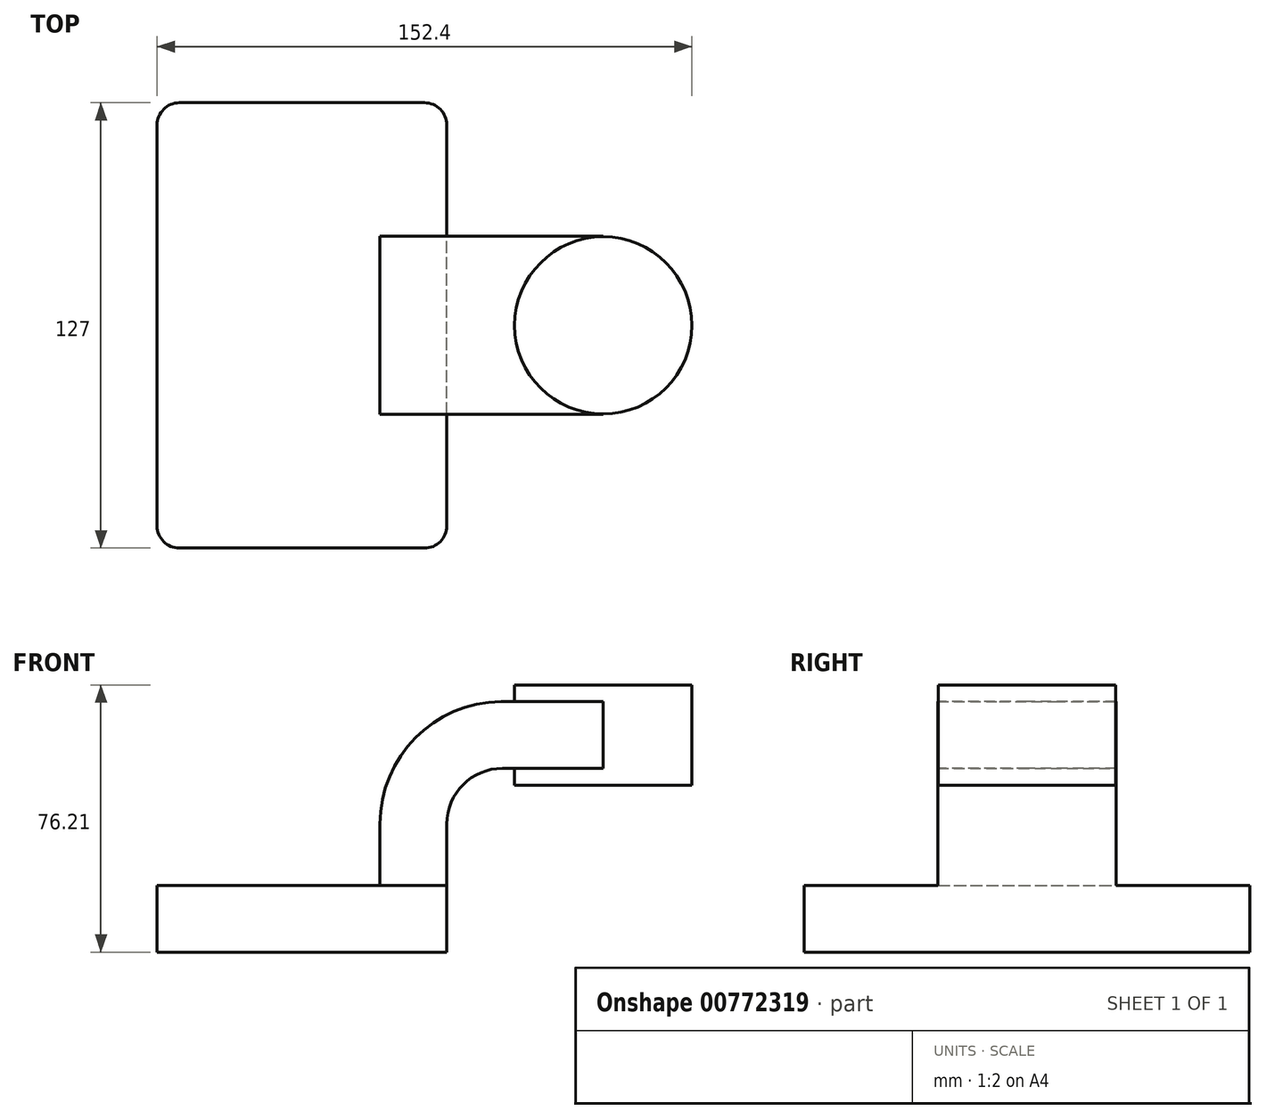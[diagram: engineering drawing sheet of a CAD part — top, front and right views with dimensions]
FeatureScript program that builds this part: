
annotation { "Feature Type Name" : "Feature", "Feature Type Description" : "" }
export const myFeature = defineFeature(function(context is Context, id is Id, definition is map)
    precondition{}
    {
        {
            var Q0;
            Q0=qCreatedBy(makeId("Front.planeOp"),FACE);
            var sketch = newSketch(context, id + "F0", { "sketchPlane" : qUnion([Q0])});
            skLineSegment(sketch, "E0.bottom", {"start": v(-41.28, 9.52) * mm, "end": v(41.27, 9.53) * mm});
            skLineSegment(sketch, "E0.top", {"start": v(-41.28, -9.52) * mm, "end": v(41.28, -9.52) * mm});
            skLineSegment(sketch, "E0.left", {"start": v(-41.28, 9.52) * mm, "end": v(-41.28, -9.53) * mm});
            skLineSegment(sketch, "E0.right", {"start": v(41.27, 9.53) * mm, "end": v(41.28, -9.52) * mm});
            skPoint(sketch, "E0.middle", {"position": v(0, 0) * mm});
            skLineSegment(sketch, "E1.bottom", {"start": v(60.32, 38.1) * mm, "end": v(111.12, 38.1) * mm});
            skLineSegment(sketch, "E1.top", {"start": v(60.32, 66.68) * mm, "end": v(111.12, 66.68) * mm});
            skLineSegment(sketch, "E1.left", {"start": v(60.32, 38.1) * mm, "end": v(60.32, 66.67) * mm});
            skLineSegment(sketch, "E1.right", {"start": v(111.12, 38.1) * mm, "end": v(111.12, 66.67) * mm});
            skPoint(sketch, "E1.middle", {"position": v(85.72, 52.39) * mm});
            skLineSegment(sketch, "E2", {"start": v(41.27, 9.53) * mm, "end": v(41.27, 27) * mm});
            skArc(sketch, "E3", {"start": v(41.27, 27) * mm, "mid": v(45.92, 38.23) * mm, "end": v(57.15, 42.88) * mm});
            skLineSegment(sketch, "E4", {"start": v(57.15, 42.88) * mm, "end": v(85.86, 42.88) * mm});
            skLineSegment(sketch, "E5.0", {"start": v(57.15, 61.93) * mm, "end": v(85.86, 61.93) * mm});
            skArc(sketch, "E5.1", {"start": v(22.22, 27) * mm, "mid": v(32.45, 51.7) * mm, "end": v(57.15, 61.93) * mm});
            skLineSegment(sketch, "E5.2", {"start": v(22.22, 9.53) * mm, "end": v(22.22, 27) * mm});
            skFitSpline(sketch, "E6", {"points": [v(-41.28, 9.53) * mm, v(57.15, 61.93) * mm], "startDerivative": vector(-0.6, 89.15) * mm, "endDerivative": vector(120.04, 0.41) * mm});
            skLineSegment(sketch, "E7", {"start": v(85.86, 38.1) * mm, "end": v(85.86, 66.68) * mm});
            skSolve(sketch);
        }
        {
            var Q0;
            Q0=makeQuery(id+"F0.imprint","IMPRINT",FACE,{"disambiguationData":[TD([[makeQuery(id+"F0.imprint","IMPRINT",EDGE,{"derivedFrom":sQuery(id+"F0.wireOp",EDGE,"E0.top")}),1.0]])]});
            extrude(context, id + "F1", {"entities" : qUnion([Q0]), "depth" : 127 * mm, "offsetDistance" : 25.4 * mm, "symmetric" : true});
        }
        {
            var Q0;
            {var subQ1=sQuery(id+"F0.wireOp",EDGE,"E2");Q0=makeQuery(id+"F0.imprint","IMPRINT",FACE,{"disambiguationData":[TD([[makeQuery(id+"F0.imprint","IMPRINT",EDGE,{"derivedFrom":subQ1}),1.0]])]});}
            var Q1;
            {var subQ0=sQuery(id+"F0.wireOp",EDGE,"E4");var subQ1=sQuery(id+"F0.wireOp",EDGE,"E1.left");var subQ2=makeQuery(id+"F0.imprint","INTERSECT",VERTEX,{"derivedFrom":[subQ1,subQ0]});Q1=makeQuery(id+"F0.imprint","IMPRINT",FACE,{"disambiguationData":[TD([[makeQuery(id+"F0.imprint","IMPRINT",EDGE,{"disambiguationData":[TD([[subQ2,-1.0]])],"derivedFrom":subQ1}),-1.0]])]});}
            extrude(context, id + "F2", {"entities" : qUnion([Q0, Q1]), "operationType" : NewBodyOperationType.ADD, "depth" : 50.8 * mm, "offsetDistance" : 25.4 * mm, "symmetric" : true});
        }
        {
            var Q0;
            {var subQ4=sQuery(id+"F0.wireOp",EDGE,"E5.1");Q0=makeQuery(id+"F0.imprint","IMPRINT",FACE,{"disambiguationData":[TD([[makeQuery(id+"F0.imprint","IMPRINT",EDGE,{"derivedFrom":subQ4}),1.0]])]});}
            extrude(context, id + "F3", {"entities" : qUnion([Q0]), "operationType" : NewBodyOperationType.ADD, "depth" : 15.88 * mm, "offsetDistance" : 25.4 * mm, "symmetric" : true});
        }
        {
            var Q0;
            {var subQ0=sQuery(id+"F0.wireOp",EDGE,"E1.right");Q0=makeQuery(id+"F0.imprint","IMPRINT",FACE,{"disambiguationData":[TD([[makeQuery(id+"F0.imprint","IMPRINT",EDGE,{"derivedFrom":subQ0}),1.0]])]});}
            var Q1;
            Q1=sQuery(id+"F0.wireOp",EDGE,"E7");
            revolve(context, id + "F4", {"operationType" : NewBodyOperationType.ADD, "surfaceOperationType" : NewSurfaceOperationType.NEW, "entities" : qUnion([Q0]), "axis" : qUnion([Q1]), "revolveType" : RevolveType.FULL});
        }
        {
            var Q0;
            Q0=makeQuery(id+"F1.opExtrude","CAP_EDGE",EDGE,{"disambiguationData":[OSD([sQuery(id+"F0.wireOp",EDGE,"E0.left")])],"isStart":false});
            var Q1;
            Q1=makeQuery(id+"F1.opExtrude","CAP_EDGE",EDGE,{"disambiguationData":[OSD([sQuery(id+"F0.wireOp",EDGE,"E0.right")])],"isStart":false});
            var Q2;
            Q2=makeQuery(id+"F1.opExtrude","CAP_EDGE",EDGE,{"disambiguationData":[OSD([sQuery(id+"F0.wireOp",EDGE,"E0.right")])],"isStart":true});
            var Q3;
            Q3=makeQuery(id+"F1.opExtrude","CAP_EDGE",EDGE,{"disambiguationData":[OSD([sQuery(id+"F0.wireOp",EDGE,"E0.left")])],"isStart":true});
            fillet(context, id + "F5", {"entities" : qUnion([Q0, Q1, Q2, Q3]), "radius" : 6.35 * mm, "tangentPropagation" : true, "allowEdgeOverflow" : false});
        }
    });
